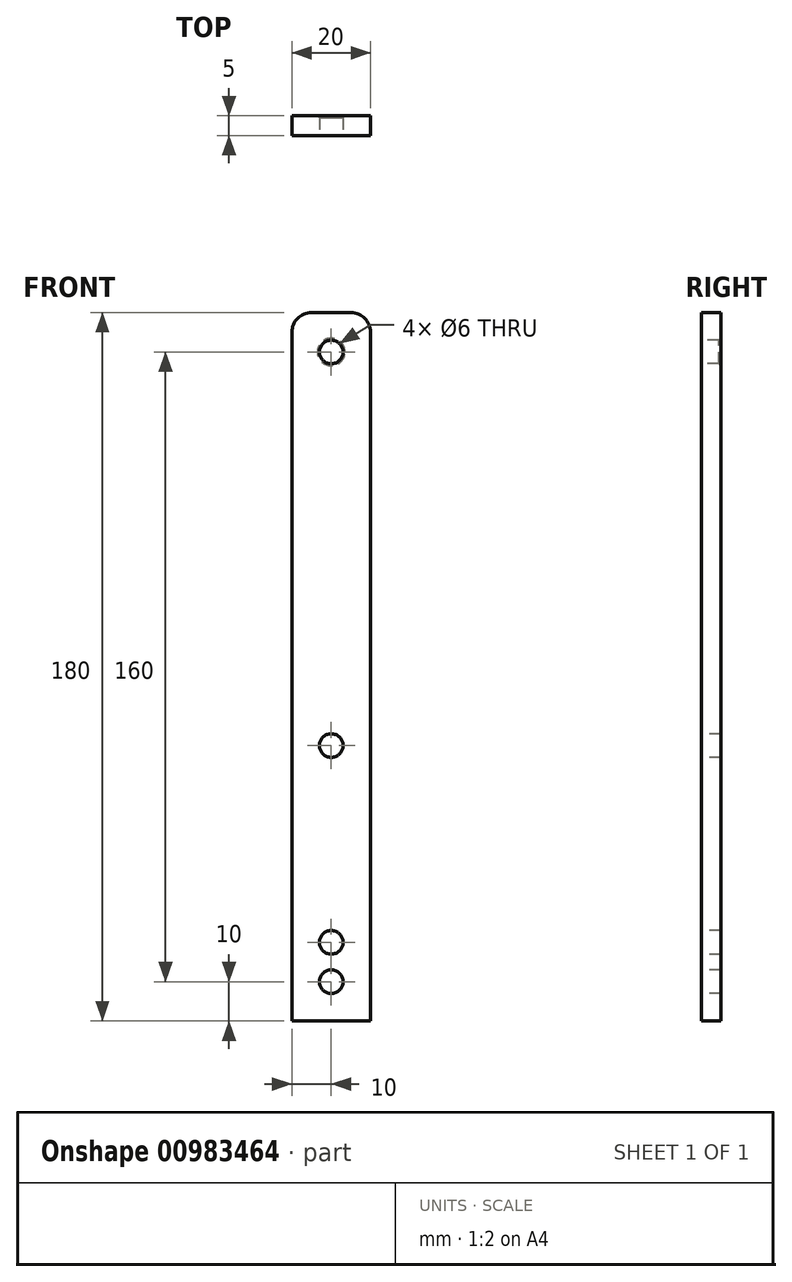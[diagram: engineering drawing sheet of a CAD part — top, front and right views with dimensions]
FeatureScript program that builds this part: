
annotation { "Feature Type Name" : "Feature", "Feature Type Description" : "" }
export const myFeature = defineFeature(function(context is Context, id is Id, definition is map)
    precondition{}
    {
        {
            var Q0;
            Q0=qCreatedBy(makeId("Front.planeOp"),FACE);
            var sketch = newSketch(context, id + "F0", { "sketchPlane" : qUnion([Q0])});
            skLineSegment(sketch, "E0.bottom", {"start": v(0, 0) * mm, "end": v(20, 0) * mm});
            skLineSegment(sketch, "E0.top", {"start": v(0, 180) * mm, "end": v(20, 180) * mm});
            skLineSegment(sketch, "E0.left", {"start": v(0, 0) * mm, "end": v(0, 180) * mm});
            skLineSegment(sketch, "E0.right", {"start": v(20, 0) * mm, "end": v(20, 180) * mm});
            skSolve(sketch);
        }
        {
            var Q0;
            Q0=qSketchRegion(id+"F0",true);
            extrude(context, id + "F1", {"entities" : qUnion([Q0]), "depth" : 5 * mm});
        }
        {
            var Q0;
            Q0=makeQuery(id+"F1.opExtrude","CAP_FACE",FACE,{"disambiguationData":[OSD([sQuery(id+"F0.wireOp",EDGE,"E0.bottom"),sQuery(id+"F0.wireOp",EDGE,"E0.top"),sQuery(id+"F0.wireOp",EDGE,"E0.left"),sQuery(id+"F0.wireOp",EDGE,"E0.right")])],"isStart":false});
            var sketch = newSketch(context, id + "F2", { "sketchPlane" : qUnion([Q0])});
            skCircle(sketch, "E1", {"center": v(10, 170) * mm, "radius": 3 * mm});
            skSolve(sketch);
        }
        {
            var Q0;
            Q0=qSketchRegion(id+"F2",true);
            extrude(context, id + "F3", {"entities" : qUnion([Q0]), "operationType" : NewBodyOperationType.REMOVE, "endBound" : BoundingType.THROUGH_ALL, "oppositeDirection" : true, "depth" : 25 * mm});
        }
        {
            var Q0;
            Q0=makeQuery(id+"F1.opExtrude","CAP_FACE",FACE,{"disambiguationData":[OSD([sQuery(id+"F0.wireOp",EDGE,"E0.bottom"),sQuery(id+"F0.wireOp",EDGE,"E0.top"),sQuery(id+"F0.wireOp",EDGE,"E0.left"),sQuery(id+"F0.wireOp",EDGE,"E0.right")])],"isStart":false});
            var sketch = newSketch(context, id + "F4", { "sketchPlane" : qUnion([Q0])});
            skLineSegment(sketch, "E2", {"start": v(10, 170) * mm, "end": v(10, 70) * mm});
            skSolve(sketch);
        }
        {
            var Q0;
            Q0=sQuery(id+"F4.wireOp",VERTEX,"E2.end");
            var Q1;
            Q1=makeQuery(id+"F1.opExtrude","SWEPT_BODY",BODY,{"disambiguationData":[OSD([sQuery(id+"F0.wireOp",EDGE,"E0.bottom"),sQuery(id+"F0.wireOp",EDGE,"E0.top"),sQuery(id+"F0.wireOp",EDGE,"E0.left"),sQuery(id+"F0.wireOp",EDGE,"E0.right")])]});
            hole(context, id + "F5", {"style" : HoleStyle.SIMPLE, "endStyle" : HoleEndStyle.THROUGH, "holeDiameter" : 6 * mm, "isTappedThrough" : true, "tappedDepth" : 12 * mm, "tapClearance" : 3, "locations" : qUnion([Q0]), "scope" : qUnion([Q1])});
        }
        {
            var Q0;
            Q0=makeQuery(id+"F1.opExtrude","CAP_FACE",FACE,{"disambiguationData":[OSD([sQuery(id+"F0.wireOp",EDGE,"E0.bottom"),sQuery(id+"F0.wireOp",EDGE,"E0.top"),sQuery(id+"F0.wireOp",EDGE,"E0.left"),sQuery(id+"F0.wireOp",EDGE,"E0.right")])],"isStart":false});
            var sketch = newSketch(context, id + "F6", { "sketchPlane" : qUnion([Q0])});
            skLineSegment(sketch, "E3", {"start": v(10, 0) * mm, "end": v(10, 10) * mm});
            skLineSegment(sketch, "E4", {"start": v(10, 10) * mm, "end": v(10, 20) * mm});
            skSolve(sketch);
        }
        {
            var Q0;
            Q0=sQuery(id+"F6.wireOp",VERTEX,"E4.start");
            var Q1;
            Q1=sQuery(id+"F6.wireOp",VERTEX,"E4.end");
            var Q2;
            Q2=makeQuery(id+"F1.opExtrude","SWEPT_BODY",BODY,{"disambiguationData":[OSD([sQuery(id+"F0.wireOp",EDGE,"E0.bottom"),sQuery(id+"F0.wireOp",EDGE,"E0.top"),sQuery(id+"F0.wireOp",EDGE,"E0.left"),sQuery(id+"F0.wireOp",EDGE,"E0.right")])]});
            hole(context, id + "F7", {"style" : HoleStyle.SIMPLE, "endStyle" : HoleEndStyle.THROUGH, "holeDiameter" : 6 * mm, "isTappedThrough" : true, "tappedDepth" : 12 * mm, "tapClearance" : 3, "locations" : qUnion([Q0, Q1]), "scope" : qUnion([Q2])});
        }
        {
            var Q0;
            Q0=makeQuery(id+"F3.boolean.opBoolean","COPY",EDGE,{"derivedFrom":makeQuery(id+"F3.opExtrude","CAP_EDGE",EDGE,{"disambiguationData":[OSD([sQuery(id+"F2.wireOp",EDGE,"E1")])],"isStart":true})});
            var Q1;
            Q1=makeQuery(id+"F3.boolean.opBoolean","INTERSECT",EDGE,{"derivedFrom":[makeQuery(id+"F1.opExtrude","CAP_FACE",FACE,{"disambiguationData":[OSD([sQuery(id+"F0.wireOp",EDGE,"E0.bottom"),sQuery(id+"F0.wireOp",EDGE,"E0.top"),sQuery(id+"F0.wireOp",EDGE,"E0.left"),sQuery(id+"F0.wireOp",EDGE,"E0.right")])],"isStart":true}),makeQuery(id+"F3.opExtrude","SWEPT_FACE",FACE,{"disambiguationData":[OSD([sQuery(id+"F2.wireOp",EDGE,"E1")])]})]});
            var Q2;
            Q2=makeQuery(id+"F5.hole-0.boolean.opBoolean","INTERSECT",EDGE,{"derivedFrom":[makeQuery(id+"F1.opExtrude","CAP_FACE",FACE,{"disambiguationData":[OSD([sQuery(id+"F0.wireOp",EDGE,"E0.bottom"),sQuery(id+"F0.wireOp",EDGE,"E0.top"),sQuery(id+"F0.wireOp",EDGE,"E0.left"),sQuery(id+"F0.wireOp",EDGE,"E0.right")])],"isStart":true}),makeQuery(id+"F5.hole-0.opRevolve","SWEPT_FACE",FACE,{"disambiguationData":[OSD([sQuery(id+"F5.hole-0.sketch.wireOp",EDGE,"core_line_2")])]})]});
            var Q3;
            Q3=makeQuery(id+"F5.hole-0.boolean.opBoolean","COPY",EDGE,{"derivedFrom":makeQuery(id+"F5.hole-0.opRevolve","SWEPT_EDGE",EDGE,{"disambiguationData":[OSD([sQuery(id+"F5.hole-0.sketch.wireOp",EDGE,"core_line_2"),sQuery(id+"F5.hole-0.sketch.wireOp",EDGE,"core_line_3")])]})});
            var Q4;
            Q4=makeQuery(id+"F7.hole-1.boolean.opBoolean","COPY",EDGE,{"derivedFrom":makeQuery(id+"F7.hole-1.opRevolve","SWEPT_EDGE",EDGE,{"disambiguationData":[OSD([sQuery(id+"F7.hole-1.sketch.wireOp",EDGE,"core_line_2"),sQuery(id+"F7.hole-1.sketch.wireOp",EDGE,"core_line_3")])]})});
            var Q5;
            Q5=makeQuery(id+"F7.hole-1.boolean.opBoolean","INTERSECT",EDGE,{"derivedFrom":[makeQuery(id+"F1.opExtrude","CAP_FACE",FACE,{"disambiguationData":[OSD([sQuery(id+"F0.wireOp",EDGE,"E0.bottom"),sQuery(id+"F0.wireOp",EDGE,"E0.top"),sQuery(id+"F0.wireOp",EDGE,"E0.left"),sQuery(id+"F0.wireOp",EDGE,"E0.right")])],"isStart":true}),makeQuery(id+"F7.hole-1.opRevolve","SWEPT_FACE",FACE,{"disambiguationData":[OSD([sQuery(id+"F7.hole-1.sketch.wireOp",EDGE,"core_line_2")])]})]});
            var Q6;
            Q6=makeQuery(id+"F7.hole-0.boolean.opBoolean","COPY",EDGE,{"derivedFrom":makeQuery(id+"F7.hole-0.opRevolve","SWEPT_EDGE",EDGE,{"disambiguationData":[OSD([sQuery(id+"F7.hole-0.sketch.wireOp",EDGE,"core_line_2"),sQuery(id+"F7.hole-0.sketch.wireOp",EDGE,"core_line_3")])]})});
            var Q7;
            Q7=makeQuery(id+"F7.hole-0.boolean.opBoolean","INTERSECT",EDGE,{"derivedFrom":[makeQuery(id+"F1.opExtrude","CAP_FACE",FACE,{"disambiguationData":[OSD([sQuery(id+"F0.wireOp",EDGE,"E0.bottom"),sQuery(id+"F0.wireOp",EDGE,"E0.top"),sQuery(id+"F0.wireOp",EDGE,"E0.left"),sQuery(id+"F0.wireOp",EDGE,"E0.right")])],"isStart":true}),makeQuery(id+"F7.hole-0.opRevolve","SWEPT_FACE",FACE,{"disambiguationData":[OSD([sQuery(id+"F7.hole-0.sketch.wireOp",EDGE,"core_line_2")])]})]});
            chamfer(context, id + "F8", {"entities" : qUnion([Q0, Q1, Q2, Q3, Q4, Q5, Q6, Q7]), "width" : 0.5 * mm, "tangentPropagation" : true});
        }
        {
            var Q0;
            Q0=makeQuery(id+"F1.opExtrude","SWEPT_EDGE",EDGE,{"disambiguationData":[OSD([sQuery(id+"F0.wireOp",EDGE,"E0.top"),sQuery(id+"F0.wireOp",EDGE,"E0.right")])]});
            var Q1;
            Q1=makeQuery(id+"F1.opExtrude","SWEPT_EDGE",EDGE,{"disambiguationData":[OSD([sQuery(id+"F0.wireOp",EDGE,"E0.top"),sQuery(id+"F0.wireOp",EDGE,"E0.left")])]});
            fillet(context, id + "F9", {"entities" : qUnion([Q0, Q1]), "radius" : 5 * mm, "tangentPropagation" : true, "allowEdgeOverflow" : false});
        }
    });
